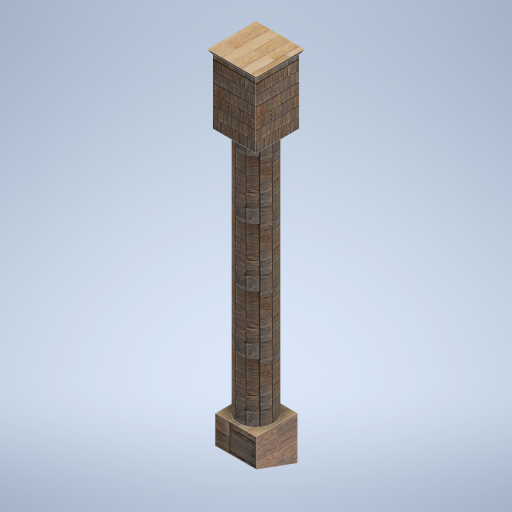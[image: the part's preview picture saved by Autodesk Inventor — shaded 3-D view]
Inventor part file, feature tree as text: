
AUTODESK INVENTOR PART (.ipt)
format: ipt  version: 2024.2 (Build 282272000, 272)  size: 352,256 bytes
history: native  units: in
note: dims shown in document units (in); Inventor stores cm internally (conversion verified against a paired STEP export)
features: sketch x5, other x3, plane x1
ambient origin geometry x8: Origin, YZ Plane, XZ Plane, XY Plane, X Axis, Y Axis, Z Axis, Center Point
bodies: Solid1 (feature_tree)
feature tree (9):
  other  "side_pillar_01_MIR2.ipt"
  other  "Solid1::side_pillar_01_MIR2.ipt"
  other  "TaggingFeature1"
  sketch  "Sketch1"  dims[d0=0.3937in]
  sketch  "Sketch2"
  sketch  "Sketch3"
  sketch  "Sketch4"
  sketch  "Sketch5"
  plane  "Work Plane3"
